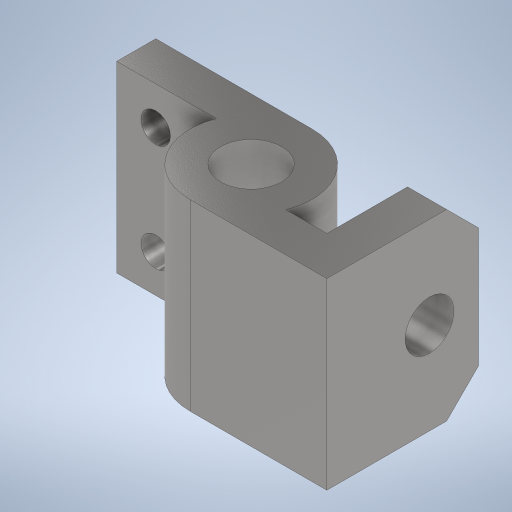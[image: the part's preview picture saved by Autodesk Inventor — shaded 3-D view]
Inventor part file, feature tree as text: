
AUTODESK INVENTOR PART (.ipt)
format: ipt  version: 2024 (Build 280153000, 153)  size: 288,256 bytes
history: native  units: mm
features: sketch x4, extrude x2, hole x2, chamfer x1
ambient origin geometry x8: Origin, YZ Plane, XZ Plane, XY Plane, X Axis, Y Axis, Z Axis, Center Point
bodies: Volumenkörper1 (feature_tree)
feature tree (9):
  extrude  "Extrusion1"  Depth=25.0mm
  extrude  "Extrusion2"  Depth=62.0mm
  chamfer  "Fasen1"  Distance=16.0mm
  hole  "Bohrung1"  [1 undecoded]
  hole  "Bohrung2"  [1 undecoded]
  sketch  "Skizze1"  dims[d0=16.0mm d1=25.0mm]
  sketch  "Skizze2"  dims[d2=62.0mm d3=56.0mm]
  sketch  "Skizze3"  dims[d4=16.0mm]
  sketch  "Skizze4"  dims[d5=120.0mm d6=16.0mm d7=25.0mm d8=75.0mm d9=0.0mm d10=25.0mm d11=75.0mm d12=0.0mm d13=13.0mm d14=2.0mm d15=45.0deg d16=20.0mm d17=6.0mm d18=4.0mm d19=2.0mm d20=90.0deg d21=8.0mm d22=20.594885mm d23=20.0mm d24=12.0mm d25=6.0mm d26=4.0mm d27=2.0mm d28=90.0deg d29=8.0mm d30=20.594885mm d31=44.0mm d32=16.0mm]
note: 2 required parameter values undecoded (feature->parameter linkage not recoverable at this tier; creation-order binding heuristic only, values carry confidence <= 0.55)
